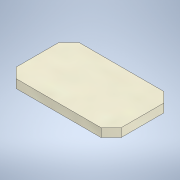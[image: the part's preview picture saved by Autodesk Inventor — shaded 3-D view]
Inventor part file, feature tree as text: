
AUTODESK INVENTOR PART (.ipt)
format: ipt  version: 2021 (Build 250183000, 183)  size: 108,544 bytes
history: native  units: mm
features: extrude x1, sketch x1
ambient origin geometry x8: Origin, YZ Plane, XZ Plane, XY Plane, X Axis, Y Axis, Z Axis, Center Point
bodies: Solid1 (feature_tree)
feature tree (2):
  extrude  "Extrusion1"  Depth=12.5mm
  sketch  "Sketch1"  dims[d0=20.9mm d1=12.5mm d2=2.0mm d3=2.0mm d10=1.7mm d11=0.0mm]
